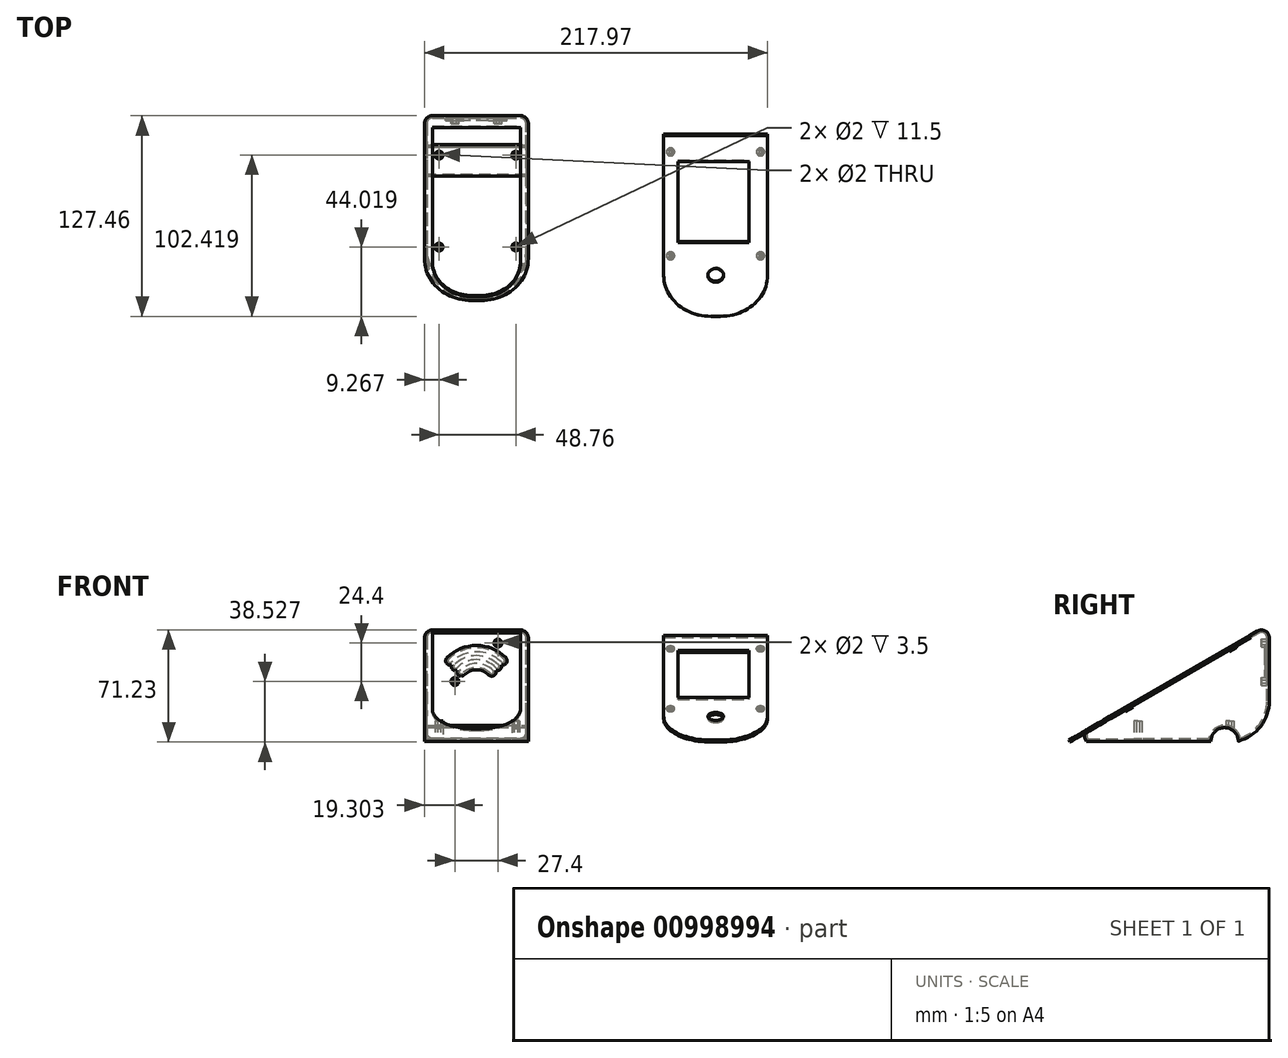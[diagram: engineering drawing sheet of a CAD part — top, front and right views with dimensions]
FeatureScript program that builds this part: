
annotation { "Feature Type Name" : "Feature", "Feature Type Description" : "" }
export const myFeature = defineFeature(function(context is Context, id is Id, definition is map)
    precondition{}
    {
        {
            var Q0;
            Q0=qCreatedBy(makeId("Front.planeOp"),FACE);
            var sketch = newSketch(context, id + "F0", { "sketchPlane" : qUnion([Q0])});
            skLineSegment(sketch, "E0", {"start": v(-25, -8.66) * mm, "end": v(-25, -48.66) * mm});
            skLineSegment(sketch, "E1", {"start": v(-25, 0) * mm, "end": v(-25, -8.66) * mm});
            skLineSegment(sketch, "E2", {"start": v(8, -4.16) * mm, "end": v(8, -51.93) * mm, "construction": true});
            skArc(sketch, "E3", {"start": v(25.68, -22.32) * mm, "mid": v(8, -15) * mm, "end": v(-9.68, -22.32) * mm});
            skArc(sketch, "E4", {"start": v(30.5, -33) * mm, "mid": v(28.8, -24.39) * mm, "end": v(23.91, -17.1) * mm, "construction": true});
            skArc(sketch, "E5", {"start": v(22.14, -25.86) * mm, "mid": v(8, -20) * mm, "end": v(-6.14, -25.86) * mm});
            skArc(sketch, "E6", {"start": v(20.37, -27.63) * mm, "mid": v(8, -22.5) * mm, "end": v(-4.37, -27.63) * mm});
            skArc(sketch, "E7", {"start": v(18.6, -29.4) * mm, "mid": v(8, -25) * mm, "end": v(-2.6, -29.4) * mm});
            skArc(sketch, "E8", {"start": v(16.84, -31.16) * mm, "mid": v(8, -27.5) * mm, "end": v(-0.84, -31.16) * mm});
            skLineSegment(sketch, "E9", {"start": v(20.5, -33) * mm, "end": v(33, -33) * mm, "construction": true});
            skPoint(sketch, "E10", {"position": v(8, -32.05) * mm});
            skArc(sketch, "E11", {"start": v(-9.68, -22.32) * mm, "mid": v(-9.68, -24.1) * mm, "end": v(-7.9, -24.1) * mm});
            skArc(sketch, "E12", {"start": v(-6.14, -25.86) * mm, "mid": v(-6.14, -27.63) * mm, "end": v(-4.37, -27.63) * mm});
            skArc(sketch, "E13", {"start": v(-2.6, -29.4) * mm, "mid": v(-2.6, -31.16) * mm, "end": v(-0.84, -31.16) * mm});
            skArc(sketch, "E14", {"start": v(16.84, -31.16) * mm, "mid": v(18.6, -31.16) * mm, "end": v(18.6, -29.4) * mm});
            skArc(sketch, "E15", {"start": v(20.37, -27.63) * mm, "mid": v(22.14, -27.63) * mm, "end": v(22.14, -25.86) * mm});
            skArc(sketch, "E16", {"start": v(23.9, -24.1) * mm, "mid": v(25.68, -24.1) * mm, "end": v(25.68, -22.32) * mm});
            skArc(sketch, "E17", {"start": v(23.9, -24.1) * mm, "mid": v(8, -17.5) * mm, "end": v(-7.9, -24.1) * mm});
            skLineSegment(sketch, "E18", {"start": v(41, 0) * mm, "end": v(-25, 0) * mm});
            skLineSegment(sketch, "E19", {"start": v(-25, -48.66) * mm, "end": v(41, -48.66) * mm});
            skLineSegment(sketch, "E20", {"start": v(41, -48.66) * mm, "end": v(41, 0) * mm});
            skCircle(sketch, "E21", {"center": v(21.7, -11.96) * mm, "radius": 1 * mm});
            skCircle(sketch, "E22", {"center": v(-5.7, -36.36) * mm, "radius": 1 * mm});
            skLineSegment(sketch, "E23.bottom", {"start": v(27.5, -4.16) * mm, "end": v(-11.5, -4.16) * mm, "construction": true});
            skLineSegment(sketch, "E23.top", {"start": v(27.5, -44.16) * mm, "end": v(-11.5, -44.16) * mm, "construction": true});
            skLineSegment(sketch, "E23.left", {"start": v(29.5, -6.16) * mm, "end": v(29.5, -42.16) * mm, "construction": true});
            skLineSegment(sketch, "E23.right", {"start": v(-13.5, -6.16) * mm, "end": v(-13.5, -42.16) * mm, "construction": true});
            skPoint(sketch, "E24.visualSharp", {"position": v(29.5, -4.16) * mm});
            skArc(sketch, "E24.filletArc", {"start": v(29.5, -6.16) * mm, "mid": v(28.92, -4.75) * mm, "end": v(27.5, -4.16) * mm, "construction": true});
            skPoint(sketch, "E25.visualSharp", {"position": v(-13.5, -4.16) * mm});
            skArc(sketch, "E25.filletArc", {"start": v(-11.5, -4.16) * mm, "mid": v(-12.91, -4.75) * mm, "end": v(-13.5, -6.16) * mm, "construction": true});
            skPoint(sketch, "E26.visualSharp", {"position": v(-13.5, -44.16) * mm});
            skArc(sketch, "E26.filletArc", {"start": v(-13.5, -42.16) * mm, "mid": v(-12.91, -43.58) * mm, "end": v(-11.5, -44.16) * mm, "construction": true});
            skPoint(sketch, "E27.visualSharp", {"position": v(29.5, -44.16) * mm});
            skArc(sketch, "E27.filletArc", {"start": v(27.5, -44.16) * mm, "mid": v(28.92, -43.58) * mm, "end": v(29.5, -42.16) * mm, "construction": true});
            skCircle(sketch, "E28.0", {"center": v(21.7, -11.96) * mm, "radius": 2.5 * mm});
            skCircle(sketch, "E29.0", {"center": v(-5.7, -36.36) * mm, "radius": 2.5 * mm});
            skSolve(sketch);
        }
        {
            var Q0;
            Q0=qCreatedBy(makeId("Right.planeOp"),FACE);
            var Q1;
            Q1=sQuery(id+"F0.wireOp",VERTEX,"E18.start");
            cPlane(context, id + "F1", {"entities" : qUnion([Q0, Q1]), "cplaneType" : CPlaneType.PLANE_POINT, "offset" : 25 * mm, "width" : 150 * mm, "height" : 150 * mm});
        }
        {
            var Q0;
            Q0=qCreatedBy(makeId("Right.planeOp"),FACE);
            var Q1;
            Q1=sQuery(id+"F0.wireOp",VERTEX,"E0.start");
            cPlane(context, id + "F2", {"entities" : qUnion([Q0, Q1]), "cplaneType" : CPlaneType.PLANE_POINT, "offset" : 25 * mm, "width" : 150 * mm, "height" : 150 * mm});
        }
        {
            var Q0;
            Q0=qCreatedBy(id+"F1.planeOp",FACE);
            var sketch = newSketch(context, id + "F3", { "sketchPlane" : qUnion([Q0])});
            skArc(sketch, "E30", {"start": v(-19.95, -74.35) * mm, "mid": v(-5.57, -64.93) * mm, "end": v(0, -48.66) * mm});
            skLineSegment(sketch, "E31", {"start": v(-19.95, -74.35) * mm, "end": v(-59.95, -74.35) * mm});
            skLineSegment(sketch, "E32", {"start": v(0, -48.66) * mm, "end": v(0, -8.66) * mm});
            skPoint(sketch, "E33.visualSharp", {"position": v(0, 0) * mm});
            skArc(sketch, "E33.filletArc", {"start": v(0, -8.66) * mm, "mid": v(-2.5, -4.33) * mm, "end": v(-7.5, -4.33) * mm});
            skLineSegment(sketch, "E34", {"start": v(-59.95, -74.35) * mm, "end": v(-117.05, -74.35) * mm});
            skLineSegment(sketch, "E35", {"start": v(-119.28, -68.86) * mm, "end": v(-119.26, -68.85) * mm});
            skPoint(sketch, "E36.visualSharp", {"position": v(-125, -74.35) * mm});
            skArc(sketch, "E36.filletArc", {"start": v(-119.26, -68.85) * mm, "mid": v(-120.02, -72.35) * mm, "end": v(-117.05, -74.35) * mm});
            skLineSegment(sketch, "E37", {"start": v(-119.28, -68.86) * mm, "end": v(-7.5, -4.33) * mm});
            skLineSegment(sketch, "E38", {"start": v(0, -28.66) * mm, "end": v(-79.15, -74.35) * mm});
            skSolve(sketch);
        }
        {
            var Q0;
            Q0=qCreatedBy(id+"F2.planeOp",FACE);
            var sketch = newSketch(context, id + "F4", { "sketchPlane" : qUnion([Q0])});
            skArc(sketch, "E39", {"start": v(-19.95, -74.35) * mm, "mid": v(-5.57, -64.93) * mm, "end": v(0, -48.66) * mm});
            skLineSegment(sketch, "E40", {"start": v(-19.95, -74.35) * mm, "end": v(-59.95, -74.35) * mm});
            skLineSegment(sketch, "E41", {"start": v(0, -48.66) * mm, "end": v(0, -8.66) * mm});
            skPoint(sketch, "E42.visualSharp", {"position": v(0, 0) * mm});
            skArc(sketch, "E42.filletArc", {"start": v(0, -8.66) * mm, "mid": v(-2.5, -4.33) * mm, "end": v(-7.5, -4.33) * mm});
            skLineSegment(sketch, "E43", {"start": v(-59.95, -74.35) * mm, "end": v(-117.05, -74.35) * mm});
            skLineSegment(sketch, "E44", {"start": v(-119.28, -68.86) * mm, "end": v(-119.26, -68.85) * mm});
            skPoint(sketch, "E45.visualSharp", {"position": v(-125, -74.35) * mm});
            skArc(sketch, "E45.filletArc", {"start": v(-119.26, -68.85) * mm, "mid": v(-120.02, -72.35) * mm, "end": v(-117.05, -74.35) * mm});
            skLineSegment(sketch, "E46", {"start": v(-119.28, -68.86) * mm, "end": v(-7.5, -4.33) * mm});
            skLineSegment(sketch, "E47", {"start": v(0, -28.66) * mm, "end": v(-79.15, -74.35) * mm});
            skSolve(sketch);
        }
        {
            var Q0;
            Q0=sQuery(id+"F3.wireOp",EDGE,"E37");
            var Q1;
            Q1=sQuery(id+"F4.wireOp",EDGE,"E46");
            cPlane(context, id + "F5", {"entities" : qUnion([Q0, Q1]), "cplaneType" : CPlaneType.LINE_ANGLE, "offset" : 25 * mm, "angle" : 0 * degree, "width" : 150 * mm, "height" : 150 * mm});
        }
        {
            var Q0;
            Q0=qCreatedBy(id+"F5.planeOp",FACE);
            var sketch = newSketch(context, id + "F6", { "sketchPlane" : qUnion([Q0])});
            skLineSegment(sketch, "E48.bottom", {"start": v(-20, 0) * mm, "end": v(36, 0) * mm});
            skLineSegment(sketch, "E48.left", {"start": v(-25, -5) * mm, "end": v(-25, -107.73) * mm});
            skLineSegment(sketch, "E48.right", {"start": v(41, -5) * mm, "end": v(41, -107.73) * mm});
            skPoint(sketch, "E49.visualSharp", {"position": v(-25, 0) * mm});
            skArc(sketch, "E49.filletArc", {"start": v(-20, 0) * mm, "mid": v(-23.53, -1.46) * mm, "end": v(-25, -5) * mm});
            skPoint(sketch, "E50.visualSharp", {"position": v(41, 0) * mm});
            skArc(sketch, "E50.filletArc", {"start": v(41, -5) * mm, "mid": v(39.54, -1.46) * mm, "end": v(36, 0) * mm});
            skPoint(sketch, "E51.orphan", {"position": v(-25, -137.73) * mm});
            skPoint(sketch, "E52.orphan", {"position": v(41, -71.81) * mm});
            skLineSegment(sketch, "E53", {"start": v(5, -137.73) * mm, "end": v(11, -137.73) * mm});
            skArc(sketch, "E54.filletArc", {"start": v(-25, -107.73) * mm, "mid": v(-16.21, -128.94) * mm, "end": v(5, -137.73) * mm});
            skPoint(sketch, "E55.visualSharp", {"position": v(41, -137.73) * mm});
            skArc(sketch, "E55.filletArc", {"start": v(11, -137.73) * mm, "mid": v(32.22, -128.94) * mm, "end": v(41, -107.73) * mm});
            skSolve(sketch);
        }
        {
            var Q0;
            Q0=qCreatedBy(makeId("Top.planeOp"),FACE);
            var Q1;
            Q1=sQuery(id+"F4.wireOp",VERTEX,"E40.end");
            cPlane(context, id + "F7", {"entities" : qUnion([Q0, Q1]), "cplaneType" : CPlaneType.PLANE_POINT, "offset" : 25 * mm, "width" : 150 * mm, "height" : 150 * mm});
        }
        {
            var Q0;
            Q0=qCreatedBy(id+"F7.planeOp",FACE);
            var sketch = newSketch(context, id + "F8", { "sketchPlane" : qUnion([Q0])});
            skArc(sketch, "E56.MirrorCS", {"start": v(-5, -79.95) * mm, "mid": v(-19.14, -74.1) * mm, "end": v(-25, -59.95) * mm, "construction": true});
            skLineSegment(sketch, "E57.MirrorCS", {"start": v(-5, -79.95) * mm, "end": v(21, -79.95) * mm, "construction": true});
            skArc(sketch, "E58.MirrorCS", {"start": v(21, -79.95) * mm, "mid": v(35.15, -74.1) * mm, "end": v(41, -59.95) * mm, "construction": true});
            skLineSegment(sketch, "E59", {"start": v(41, -59.95) * mm, "end": v(41, -59.95) * mm});
            skArc(sketch, "E60.MirrorCS", {"start": v(-5, -39.95) * mm, "mid": v(-19.14, -45.8) * mm, "end": v(-25, -59.95) * mm, "construction": true});
            skLineSegment(sketch, "E61.MirrorCS", {"start": v(-5, -39.95) * mm, "end": v(21, -39.95) * mm, "construction": true});
            skArc(sketch, "E62.MirrorCS", {"start": v(21, -39.95) * mm, "mid": v(35.15, -45.8) * mm, "end": v(41, -59.95) * mm, "construction": true});
            skArc(sketch, "E63", {"start": v(-25, -93.73) * mm, "mid": v(8, -109.08) * mm, "end": v(41, -93.73) * mm});
            skLineSegment(sketch, "E64", {"start": v(-25, -93.73) * mm, "end": v(-25, -59.95) * mm});
            skLineSegment(sketch, "E65", {"start": v(41, -93.73) * mm, "end": v(41, -59.95) * mm});
            skLineSegment(sketch, "E66", {"start": v(41, -59.95) * mm, "end": v(41, -19.49) * mm});
            skLineSegment(sketch, "E67", {"start": v(41, -19.49) * mm, "end": v(-25, -19.49) * mm});
            skLineSegment(sketch, "E68", {"start": v(-25, -19.49) * mm, "end": v(-25, -59.95) * mm});
            skLineSegment(sketch, "E69.bottom", {"start": v(-19.35, -95.3) * mm, "end": v(36.65, -95.3) * mm, "construction": true});
            skLineSegment(sketch, "E69.top", {"start": v(-19.35, -11.3) * mm, "end": v(36.65, -11.3) * mm, "construction": true});
            skLineSegment(sketch, "E69.left", {"start": v(-19.35, -95.3) * mm, "end": v(-19.35, -11.3) * mm, "construction": true});
            skLineSegment(sketch, "E69.right", {"start": v(36.65, -95.3) * mm, "end": v(36.65, -11.3) * mm, "construction": true});
            skLineSegment(sketch, "E70.bottom", {"start": v(-17.35, -87.06) * mm, "end": v(34.65, -87.06) * mm, "construction": true});
            skLineSegment(sketch, "E70.top", {"start": v(-17.35, -3.06) * mm, "end": v(34.65, -3.06) * mm, "construction": true});
            skLineSegment(sketch, "E70.left", {"start": v(-19.35, -85.06) * mm, "end": v(-19.35, -5.06) * mm, "construction": true});
            skLineSegment(sketch, "E70.right", {"start": v(36.65, -85.06) * mm, "end": v(36.65, -5.06) * mm, "construction": true});
            skCircle(sketch, "E71", {"center": v(-15.73, -83.44) * mm, "radius": 1 * mm});
            skCircle(sketch, "E72", {"center": v(33.03, -83.44) * mm, "radius": 1 * mm});
            skCircle(sketch, "E73", {"center": v(33.03, -25.04) * mm, "radius": 1 * mm});
            skCircle(sketch, "E74", {"center": v(-15.73, -25.04) * mm, "radius": 1 * mm});
            skPoint(sketch, "E75.visualSharp", {"position": v(-19.35, -87.06) * mm});
            skArc(sketch, "E75.filletArc", {"start": v(-19.35, -85.06) * mm, "mid": v(-18.77, -86.47) * mm, "end": v(-17.35, -87.06) * mm, "construction": true});
            skPoint(sketch, "E76.visualSharp", {"position": v(-19.35, -3.06) * mm});
            skArc(sketch, "E76.filletArc", {"start": v(-17.35, -3.06) * mm, "mid": v(-18.77, -3.65) * mm, "end": v(-19.35, -5.06) * mm, "construction": true});
            skPoint(sketch, "E77.visualSharp", {"position": v(36.65, -87.06) * mm});
            skArc(sketch, "E77.filletArc", {"start": v(34.65, -87.06) * mm, "mid": v(36.06, -86.47) * mm, "end": v(36.65, -85.06) * mm, "construction": true});
            skPoint(sketch, "E78.visualSharp", {"position": v(36.65, -3.06) * mm});
            skArc(sketch, "E78.filletArc", {"start": v(36.65, -5.06) * mm, "mid": v(36.06, -3.65) * mm, "end": v(34.65, -3.06) * mm, "construction": true});
            skCircle(sketch, "E79", {"center": v(-15.73, -83.44) * mm, "radius": 2.5 * mm});
            skCircle(sketch, "E80", {"center": v(33.03, -83.44) * mm, "radius": 2.5 * mm});
            skCircle(sketch, "E81", {"center": v(33.03, -25.04) * mm, "radius": 2.5 * mm});
            skCircle(sketch, "E82", {"center": v(-15.73, -25.04) * mm, "radius": 2.5 * mm});
            skSolve(sketch);
        }
        {
            var Q0;
            {var subQ1=sQuery(id+"F3.wireOp",EDGE,"E30");Q0=makeQuery(id+"F3.imprint","IMPRINT",FACE,{"disambiguationData":[TD([[makeQuery(id+"F3.imprint","IMPRINT",EDGE,{"derivedFrom":subQ1}),1.0]])]});}
            var Q1;
            {var subQ1=sQuery(id+"F4.wireOp",EDGE,"E39");Q1=makeQuery(id+"F4.imprint","IMPRINT",FACE,{"disambiguationData":[TD([[makeQuery(id+"F4.imprint","IMPRINT",EDGE,{"derivedFrom":subQ1}),1.0]])]});}
            loft(context, id + "F9", {"sheetProfilesArray" : [{ "sheetProfileEntities" : qUnion([Q0]) }, { "sheetProfileEntities" : qUnion([Q1]) }]});
        }
        {
            var Q1;
            {var subQ5=sQuery(id+"F4.wireOp",EDGE,"E42.filletArc");Q1=makeQuery(id+"F4.imprint","IMPRINT",FACE,{"disambiguationData":[TD([[makeQuery(id+"F4.imprint","IMPRINT",EDGE,{"derivedFrom":subQ5}),1.0]])]});}
            var Q2;
            {var subQ5=sQuery(id+"F3.wireOp",EDGE,"E33.filletArc");Q2=makeQuery(id+"F3.imprint","IMPRINT",FACE,{"disambiguationData":[TD([[makeQuery(id+"F3.imprint","IMPRINT",EDGE,{"derivedFrom":subQ5}),1.0]])]});}
            var Q3;
            Q3=sQuery(id+"F8.wireOp",EDGE,"E63");
            loft(context, id + "F10", {"operationType" : NewBodyOperationType.ADD, "addGuides" : true, "sheetProfilesArray" : [{ "sheetProfileEntities" : qUnion([Q1]) }, { "sheetProfileEntities" : qUnion([Q2]) }], "guidesArray" : [{ "guideEntities" : qUnion([Q3]), "guideDerivativeType" : LoftGuideDerivativeType.DEFAULT, "guideDerivativeMagnitude" : 1 }]});
        }
        {
            var Q0;
            Q0=makeQuery(id+"F0.imprint","IMPRINT",FACE,{"disambiguationData":[TD([[makeQuery(id+"F0.imprint","IMPRINT",EDGE,{"derivedFrom":sQuery(id+"F0.wireOp",EDGE,"E3")}),1.0]])]});
            var Q1;
            Q1=makeQuery(id+"F0.imprint","IMPRINT",FACE,{"disambiguationData":[TD([[makeQuery(id+"F0.imprint","IMPRINT",EDGE,{"derivedFrom":sQuery(id+"F0.wireOp",EDGE,"E5")}),1.0]])]});
            var Q2;
            Q2=makeQuery(id+"F0.imprint","IMPRINT",FACE,{"disambiguationData":[TD([[makeQuery(id+"F0.imprint","IMPRINT",EDGE,{"derivedFrom":sQuery(id+"F0.wireOp",EDGE,"E7")}),1.0]])]});
            extrude(context, id + "F11", {"entities" : qUnion([Q0, Q1, Q2]), "operationType" : NewBodyOperationType.REMOVE, "depth" : 1.5 * mm, "offsetDistance" : 25 * mm});
        }
        {
            var Q0;
            Q0=makeQuery(id+"F6.imprint","IMPRINT",FACE,{"disambiguationData":[TD([[makeQuery(id+"F6.imprint","IMPRINT",EDGE,{"derivedFrom":sQuery(id+"F6.wireOp",EDGE,"E48.bottom")}),-1.0]])]});
            var Q1;
            Q1=makeQuery(id+"F9.opLoft","SWEPT_FACE",FACE,{"disambiguationData":[OSD([sQuery(id+"F3.wireOp",EDGE,"E30"),sQuery(id+"F3.wireOp",EDGE,"E31"),sQuery(id+"F3.wireOp",EDGE,"E34"),sQuery(id+"F3.wireOp",EDGE,"E36.filletArc"),sQuery(id+"FAEsRkGbxnJ1MBX.wireOp",EDGE,"a8245fd8-4850-4980-bf5e-810671c84981"),sQuery(id+"FAEsRkGbxnJ1MBX.wireOp",EDGE,"8b04b0c7-bf4b-4598-bf27-2dfc9577b658"),sQuery(id+"FAEsRkGbxnJ1MBX.wireOp",EDGE,"FveUAupK-Kzv4-wpNj-ClBy-OwDI9axHzK4t"),sQuery(id+"FAEsRkGbxnJ1MBX.wireOp",EDGE,"3c92983d-d9bb-4d16-bbb1-dd7e6bf06c28.filletArc")])]});
            extrude(context, id + "F12", {"entities" : qUnion([Q0]), "operationType" : NewBodyOperationType.INTERSECT, "endBound" : BoundingType.UP_TO_SURFACE, "oppositeDirection" : true, "depth" : 25 * mm, "endBoundEntityFace" : qUnion([Q1]), "offsetDistance" : 25 * mm});
        }
        {
            var Q0;
            Q0=qCreatedBy(makeId("Right.planeOp"),FACE);
            var sketch = newSketch(context, id + "F13", { "sketchPlane" : qUnion([Q0])});
            skArc(sketch, "E83", {"start": v(-19.79, -74.35) * mm, "mid": v(-28.43, -65.7) * mm, "end": v(-37.08, -74.35) * mm});
            skPoint(sketch, "E84.center.orphan", {"position": v(-38.01, -74.35) * mm});
            skLineSegment(sketch, "E85", {"start": v(-19.79, -74.35) * mm, "end": v(-37.08, -74.35) * mm});
            skSolve(sketch);
        }
        {
            var Q0;
            Q0=makeQuery(id+"F13.imprint","IMPRINT",FACE,{"disambiguationData":[TD([[makeQuery(id+"F13.imprint","IMPRINT",EDGE,{"derivedFrom":sQuery(id+"F13.wireOp",EDGE,"E83")}),1.0]])]});
            extrude(context, id + "F14", {"entities" : qUnion([Q0]), "operationType" : NewBodyOperationType.REMOVE, "oppositeDirection" : true, "depth" : 90 * mm, "offsetDistance" : 25 * mm, "symmetric" : true});
        }
        {
            var Q0;
            Q0=makeQuery(id+"F10.opLoft","MID_CAP_EDGE",EDGE,{"disambiguationData":[OSD([sQuery(id+"F3.wireOp",EDGE,"E33.filletArc"),sQuery(id+"F3.wireOp",EDGE,"E36.filletArc"),sQuery(id+"F3.wireOp",EDGE,"E37")])],"capPos":1.0});
            var Q1;
            Q1=makeQuery(id+"F12.boolean.opBoolean","COPY",EDGE,{"derivedFrom":makeQuery(id+"F12.boolean.toolComplement.opBoolean","COPY",EDGE,{"derivedFrom":makeQuery(id+"F12.opExtrude","CAP_EDGE",EDGE,{"disambiguationData":[OSD([sQuery(id+"F6.wireOp",EDGE,"E55.filletArc")])],"isStart":true})})});
            var Q2;
            Q2=makeQuery(id+"F12.boolean.opBoolean","MERGE",EDGE,{"derivedFrom":[makeQuery(id+"F10.opLoft","SWEPT_EDGE",EDGE,{"disambiguationData":[OSD([sQuery(id+"F3.wireOp",EDGE,"E36.filletArc"),sQuery(id+"F3.wireOp",EDGE,"E37"),sQuery(id+"F4.wireOp",EDGE,"E45.filletArc"),sQuery(id+"F4.wireOp",EDGE,"E46")])]})],"fromTools":[makeQuery(id+"F12.boolean.toolComplement.opBoolean","COPY",EDGE,{"derivedFrom":makeQuery(id+"F12.opExtrude","CAP_EDGE",EDGE,{"disambiguationData":[OSD([sQuery(id+"F6.wireOp",EDGE,"E53")])],"isStart":true})})]});
            fillet(context, id + "F15", {"entities" : qUnion([Q0, Q1, Q2]), "radius" : 5 * mm, "tangentPropagation" : true, "allowEdgeOverflow" : false});
        }
        {
            var Q0;
            Q0=makeQuery(id+"F10.opLoft","SWEPT_FACE",FACE,{"disambiguationData":[OSD([sQuery(id+"F3.wireOp",EDGE,"E33.filletArc"),sQuery(id+"F3.wireOp",EDGE,"E36.filletArc"),sQuery(id+"F3.wireOp",EDGE,"E37"),sQuery(id+"F4.wireOp",EDGE,"E42.filletArc"),sQuery(id+"F4.wireOp",EDGE,"E45.filletArc"),sQuery(id+"F4.wireOp",EDGE,"E46")])]});
            shell(context, id + "F16", {"entities" : qUnion([Q0]), "thickness" : 1.5 * mm});
        }
        {
            var Q0;
            Q0=makeQuery(id+"F8.imprint","IMPRINT",FACE,{"disambiguationData":[TD([[makeQuery(id+"F8.imprint","IMPRINT",EDGE,{"derivedFrom":sQuery(id+"F8.wireOp",EDGE,"E73")}),-1.0]])]});
            var Q1;
            Q1=makeQuery(id+"F8.imprint","IMPRINT",FACE,{"disambiguationData":[TD([[makeQuery(id+"F8.imprint","IMPRINT",EDGE,{"derivedFrom":sQuery(id+"F8.wireOp",EDGE,"E74")}),-1.0]])]});
            var Q2;
            Q2=makeQuery(id+"F8.imprint","IMPRINT",FACE,{"disambiguationData":[TD([[makeQuery(id+"F8.imprint","IMPRINT",EDGE,{"derivedFrom":sQuery(id+"F8.wireOp",EDGE,"E71")}),-1.0]])]});
            var Q3;
            Q3=makeQuery(id+"F8.imprint","IMPRINT",FACE,{"disambiguationData":[TD([[makeQuery(id+"F8.imprint","IMPRINT",EDGE,{"derivedFrom":sQuery(id+"F8.wireOp",EDGE,"E72")}),-1.0]])]});
            extrude(context, id + "F17", {"entities" : qUnion([Q0, Q1, Q2, Q3]), "operationType" : NewBodyOperationType.ADD, "depth" : 13 * mm, "offsetDistance" : 25 * mm});
        }
        {
            var Q0;
            Q0=makeQuery(id+"F8.imprint","IMPRINT",FACE,{"disambiguationData":[TD([[makeQuery(id+"F8.imprint","IMPRINT",EDGE,{"derivedFrom":sQuery(id+"F8.wireOp",EDGE,"E74")}),-1.0]])]});
            var Q1;
            Q1=makeQuery(id+"F8.imprint","IMPRINT",FACE,{"disambiguationData":[TD([[makeQuery(id+"F8.imprint","IMPRINT",EDGE,{"derivedFrom":sQuery(id+"F8.wireOp",EDGE,"E73")}),-1.0]])]});
            var Q2;
            Q2=makeQuery(id+"F14.boolean.opBoolean","COPY",FACE,{"derivedFrom":makeQuery(id+"F14.opExtrude","SWEPT_FACE",FACE,{"disambiguationData":[OSD([sQuery(id+"F13.wireOp",EDGE,"E83")])]})});
            var Q3;
            {var subQ1=sQuery(id+"F4.wireOp",EDGE,"E39");var subQ6=sQuery(id+"F3.wireOp",EDGE,"E30");Q3=makeQuery(id+"F14.boolean.opBoolean","SPLIT",BODY,{"disambiguationData":[OD(0.0)],"derivedFrom":makeQuery(id+"F9.opLoft","SWEPT_BODY",BODY,{"disambiguationData":[OSD([makeQuery(id+"F3.imprint","IMPRINT",FACE,{"disambiguationData":[TD([[makeQuery(id+"F3.imprint","IMPRINT",EDGE,{"derivedFrom":subQ6}),1.0]])]}),makeQuery(id+"F4.imprint","IMPRINT",FACE,{"disambiguationData":[TD([[makeQuery(id+"F4.imprint","IMPRINT",EDGE,{"derivedFrom":subQ1}),1.0]])]})])]})});}
            extrude(context, id + "F18", {"entities" : qUnion([Q0, Q1]), "operationType" : NewBodyOperationType.REMOVE, "endBound" : BoundingType.UP_TO_SURFACE, "depth" : 25 * mm, "endBoundEntityFace" : qUnion([Q2]), "endBoundEntityBody" : qUnion([Q3]), "offsetDistance" : 25 * mm});
        }
        {
            var Q0;
            Q0=qCreatedBy(id+"F5.planeOp",FACE);
            var sketch = newSketch(context, id + "F19", { "sketchPlane" : qUnion([Q0])});
            skLineSegment(sketch, "E86.bottom", {"start": v(131.97, -9.45) * mm, "end": v(187.97, -9.45) * mm, "construction": true});
            skLineSegment(sketch, "E86.left", {"start": v(126.97, -14.45) * mm, "end": v(126.97, -117.18) * mm});
            skLineSegment(sketch, "E86.right", {"start": v(192.97, -14.45) * mm, "end": v(192.97, -117.18) * mm});
            skPoint(sketch, "E87.visualSharp", {"position": v(126.97, -9.45) * mm});
            skArc(sketch, "E87.filletArc", {"start": v(131.97, -9.45) * mm, "mid": v(128.43, -10.92) * mm, "end": v(126.97, -14.45) * mm, "construction": true});
            skPoint(sketch, "E88.visualSharp", {"position": v(192.97, -9.45) * mm});
            skArc(sketch, "E88.filletArc", {"start": v(192.97, -14.45) * mm, "mid": v(191.5, -10.92) * mm, "end": v(187.97, -9.45) * mm, "construction": true});
            skPoint(sketch, "E89.orphan", {"position": v(126.97, -147.18) * mm});
            skPoint(sketch, "E90.orphan", {"position": v(192.97, -81.27) * mm});
            skLineSegment(sketch, "E91", {"start": v(156.97, -147.18) * mm, "end": v(162.97, -147.18) * mm});
            skArc(sketch, "E92.filletArc", {"start": v(126.97, -117.18) * mm, "mid": v(135.75, -138.4) * mm, "end": v(156.97, -147.18) * mm});
            skPoint(sketch, "E93.visualSharp", {"position": v(192.97, -147.18) * mm});
            skArc(sketch, "E93.filletArc", {"start": v(162.97, -147.18) * mm, "mid": v(184.18, -138.4) * mm, "end": v(192.97, -117.18) * mm});
            skLineSegment(sketch, "E94.bottom", {"start": v(128.74, -25.19) * mm, "end": v(190.97, -25.19) * mm, "construction": true});
            skLineSegment(sketch, "E94.top", {"start": v(128.74, -106.47) * mm, "end": v(190.97, -106.47) * mm, "construction": true});
            skLineSegment(sketch, "E94.left", {"start": v(128.74, -25.19) * mm, "end": v(128.74, -106.47) * mm, "construction": true});
            skLineSegment(sketch, "E94.right", {"start": v(190.97, -25.19) * mm, "end": v(190.97, -106.47) * mm, "construction": true});
            skCircle(sketch, "E95", {"center": v(131.28, -27.73) * mm, "radius": 1 * mm});
            skCircle(sketch, "E96", {"center": v(188.43, -27.73) * mm, "radius": 1 * mm});
            skCircle(sketch, "E97", {"center": v(131.28, -103.93) * mm, "radius": 1 * mm});
            skCircle(sketch, "E98", {"center": v(188.43, -103.93) * mm, "radius": 1 * mm});
            skCircle(sketch, "E99", {"center": v(159.97, -117.18) * mm, "radius": 5 * mm});
            skLineSegment(sketch, "E100.bottom", {"start": v(135.93, -33.57) * mm, "end": v(181.14, -33.57) * mm});
            skLineSegment(sketch, "E100.top", {"start": v(135.93, -93) * mm, "end": v(181.14, -93) * mm});
            skLineSegment(sketch, "E100.left", {"start": v(135.93, -33.57) * mm, "end": v(135.93, -93) * mm});
            skLineSegment(sketch, "E100.right", {"start": v(181.14, -33.57) * mm, "end": v(181.14, -93) * mm});
            skLineSegment(sketch, "E101.0", {"start": v(133.96, -31.6) * mm, "end": v(184.76, -31.6) * mm, "construction": true});
            skLineSegment(sketch, "E101.1", {"start": v(133.96, -31.6) * mm, "end": v(133.96, -93.5) * mm, "construction": true});
            skLineSegment(sketch, "E101.2", {"start": v(133.96, -93.5) * mm, "end": v(184.76, -93.5) * mm, "construction": true});
            skLineSegment(sketch, "E101.3", {"start": v(184.76, -31.6) * mm, "end": v(184.76, -93.5) * mm, "construction": true});
            skLineSegment(sketch, "E102", {"start": v(126.97, -14.45) * mm, "end": v(192.97, -14.45) * mm});
            skLineSegment(sketch, "E103.bottom", {"start": v(237.11, -106.82) * mm, "end": v(289.11, -106.82) * mm, "construction": true});
            skLineSegment(sketch, "E103.top", {"start": v(237.11, -22.82) * mm, "end": v(289.11, -22.82) * mm, "construction": true});
            skLineSegment(sketch, "E103.left", {"start": v(235.11, -104.82) * mm, "end": v(235.11, -24.82) * mm, "construction": true});
            skLineSegment(sketch, "E103.right", {"start": v(291.11, -104.82) * mm, "end": v(291.11, -24.82) * mm, "construction": true});
            skCircle(sketch, "E104", {"center": v(238.73, -103.2) * mm, "radius": 1.5 * mm});
            skCircle(sketch, "E105", {"center": v(287.5, -103.2) * mm, "radius": 1.5 * mm});
            skCircle(sketch, "E106", {"center": v(287.5, -44.8) * mm, "radius": 1.5 * mm});
            skCircle(sketch, "E107", {"center": v(238.73, -44.8) * mm, "radius": 1.5 * mm});
            skPoint(sketch, "E108.visualSharp", {"position": v(235.11, -106.82) * mm});
            skArc(sketch, "E108.filletArc", {"start": v(235.11, -104.82) * mm, "mid": v(235.7, -106.24) * mm, "end": v(237.11, -106.82) * mm, "construction": true});
            skPoint(sketch, "E109.visualSharp", {"position": v(235.11, -22.82) * mm});
            skArc(sketch, "E109.filletArc", {"start": v(237.11, -22.82) * mm, "mid": v(235.7, -23.4) * mm, "end": v(235.11, -24.82) * mm, "construction": true});
            skPoint(sketch, "E110.visualSharp", {"position": v(291.11, -106.82) * mm});
            skArc(sketch, "E110.filletArc", {"start": v(289.11, -106.82) * mm, "mid": v(290.53, -106.24) * mm, "end": v(291.11, -104.82) * mm, "construction": true});
            skPoint(sketch, "E111.visualSharp", {"position": v(291.11, -22.82) * mm});
            skArc(sketch, "E111.filletArc", {"start": v(291.11, -24.82) * mm, "mid": v(290.53, -23.4) * mm, "end": v(289.11, -22.82) * mm, "construction": true});
            skCircle(sketch, "E112.0", {"center": v(131.28, -103.93) * mm, "radius": 2.5 * mm});
            skCircle(sketch, "E113.0", {"center": v(188.43, -103.93) * mm, "radius": 2.5 * mm});
            skCircle(sketch, "E114.0", {"center": v(131.28, -27.73) * mm, "radius": 2.5 * mm});
            skCircle(sketch, "E115.0", {"center": v(188.43, -27.73) * mm, "radius": 2.5 * mm});
            skSolve(sketch);
        }
        {
            var Q0;
            Q0=makeQuery(id+"F19.imprint","IMPRINT",FACE,{"disambiguationData":[TD([[makeQuery(id+"F19.imprint","IMPRINT",EDGE,{"derivedFrom":sQuery(id+"F19.wireOp",EDGE,"E86.left")}),1.0]])]});
            var Q1;
            Q1=makeQuery(id+"F19.imprint","IMPRINT",FACE,{"disambiguationData":[TD([[makeQuery(id+"F19.imprint","IMPRINT",EDGE,{"derivedFrom":sQuery(id+"F19.wireOp",EDGE,"E95")}),1.0]])]});
            var Q2;
            Q2=makeQuery(id+"F19.imprint","IMPRINT",FACE,{"disambiguationData":[TD([[makeQuery(id+"F19.imprint","IMPRINT",EDGE,{"derivedFrom":sQuery(id+"F19.wireOp",EDGE,"E96")}),1.0]])]});
            var Q3;
            Q3=makeQuery(id+"F19.imprint","IMPRINT",FACE,{"disambiguationData":[TD([[makeQuery(id+"F19.imprint","IMPRINT",EDGE,{"derivedFrom":sQuery(id+"F19.wireOp",EDGE,"E98")}),1.0]])]});
            var Q4;
            Q4=makeQuery(id+"F19.imprint","IMPRINT",FACE,{"disambiguationData":[TD([[makeQuery(id+"F19.imprint","IMPRINT",EDGE,{"derivedFrom":sQuery(id+"F19.wireOp",EDGE,"E97")}),1.0]])]});
            var Q5;
            Q5=makeQuery(id+"F19.imprint","IMPRINT",FACE,{"disambiguationData":[TD([[makeQuery(id+"F19.imprint","IMPRINT",EDGE,{"derivedFrom":sQuery(id+"F19.wireOp",EDGE,"E97")}),-1.0]])]});
            var Q6;
            Q6=makeQuery(id+"F19.imprint","IMPRINT",FACE,{"disambiguationData":[TD([[makeQuery(id+"F19.imprint","IMPRINT",EDGE,{"derivedFrom":sQuery(id+"F19.wireOp",EDGE,"E98")}),-1.0]])]});
            var Q7;
            Q7=makeQuery(id+"F19.imprint","IMPRINT",FACE,{"disambiguationData":[TD([[makeQuery(id+"F19.imprint","IMPRINT",EDGE,{"derivedFrom":sQuery(id+"F19.wireOp",EDGE,"E95")}),-1.0]])]});
            var Q8;
            Q8=makeQuery(id+"F19.imprint","IMPRINT",FACE,{"disambiguationData":[TD([[makeQuery(id+"F19.imprint","IMPRINT",EDGE,{"derivedFrom":sQuery(id+"F19.wireOp",EDGE,"E96")}),-1.0]])]});
            extrude(context, id + "F20", {"entities" : qUnion([Q0, Q1, Q2, Q3, Q4, Q5, Q6, Q7, Q8]), "oppositeDirection" : true, "depth" : 1.5 * mm, "offsetDistance" : 25 * mm});
        }
        {
            var Q0;
            Q0=makeQuery(id+"F19.imprint","IMPRINT",FACE,{"disambiguationData":[TD([[makeQuery(id+"F19.imprint","IMPRINT",EDGE,{"derivedFrom":sQuery(id+"F19.wireOp",EDGE,"E97")}),-1.0]])]});
            var Q1;
            Q1=makeQuery(id+"F19.imprint","IMPRINT",FACE,{"disambiguationData":[TD([[makeQuery(id+"F19.imprint","IMPRINT",EDGE,{"derivedFrom":sQuery(id+"F19.wireOp",EDGE,"E96")}),-1.0]])]});
            var Q2;
            Q2=makeQuery(id+"F19.imprint","IMPRINT",FACE,{"disambiguationData":[TD([[makeQuery(id+"F19.imprint","IMPRINT",EDGE,{"derivedFrom":sQuery(id+"F19.wireOp",EDGE,"E98")}),-1.0]])]});
            var Q3;
            Q3=makeQuery(id+"F19.imprint","IMPRINT",FACE,{"disambiguationData":[TD([[makeQuery(id+"F19.imprint","IMPRINT",EDGE,{"derivedFrom":sQuery(id+"F19.wireOp",EDGE,"E95")}),-1.0]])]});
            extrude(context, id + "F21", {"entities" : qUnion([Q0, Q1, Q2, Q3]), "operationType" : NewBodyOperationType.ADD, "oppositeDirection" : true, "depth" : 2.5 * mm, "offsetDistance" : 25 * mm});
        }
        {
            var Q0;
            Q0=makeQuery(id+"F0.imprint","IMPRINT",FACE,{"disambiguationData":[TD([[makeQuery(id+"F0.imprint","IMPRINT",EDGE,{"derivedFrom":sQuery(id+"F0.wireOp",EDGE,"E21")}),-1.0]])]});
            var Q1;
            Q1=makeQuery(id+"F0.imprint","IMPRINT",FACE,{"disambiguationData":[TD([[makeQuery(id+"F0.imprint","IMPRINT",EDGE,{"derivedFrom":sQuery(id+"F0.wireOp",EDGE,"E22")}),-1.0]])]});
            extrude(context, id + "F22", {"entities" : qUnion([Q0, Q1]), "operationType" : NewBodyOperationType.ADD, "depth" : 5 * mm, "offsetDistance" : 25 * mm});
        }
    });
